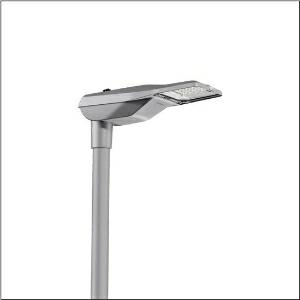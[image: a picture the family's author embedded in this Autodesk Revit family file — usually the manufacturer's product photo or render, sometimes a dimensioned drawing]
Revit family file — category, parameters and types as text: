
# Revit family: streetlight_sl_21_iq_micro___p0_5a_5xe1v31v08cb_beee
name_source: partatom
category: Lighting Fixtures
units: mm (PartAtom-declared; Revit-internal decimal feet)

## family parameters
Cut with Voids When Loaded = No
Host = Face
Light Source = No
Part Type = Normal
Room Calculation Point = No
Round Connector Dimension = Use Diameter
Shared = No

## types (1)
- --- (1 x LED, 2840 lm, 19.1 W, 3000K)
    Apparent Load = 19 VA
    CIE Flux Codes = 37 73 96 100 100
    Color Rendering = 70
    Color Temperature = 3000K
    Default Elevation = 1800 mm
    Description = Streetlight SL 21 iQ micro, mast luminaire, primary light control with lens, of PMMA, primary optical cover: cover, of toughened safety glass, transparent, light distribution: P0.5a, light emission: direct distribution, primary light characteristic: asymmetric, installation type: post-top, side-entry, LED, High Power LED, rated luminous flux: 2.840lm, luminous efficacy: 149lm/W, light colour: 730, colour temperature: 3000K, control gear: iQ-Street Remote, D4i with power reduction, control: pre-setting: logarithmic dimming characteristic, Street-Remote, Auto-Match, Temp-Guard, Lumen-Switch, Night-Set, Smart-Wire, Light-Fading, Desk-Remote (wireless, voltage-free reading and setting of iQ features in the workshop via application-optimized NFC function/RFID function), optimised constant luminous flux control (CLO 2.0), mains connection: 220..240V, AC, 50/60Hz, start of lifetime: 19W, end of service life: 20W, reduction: 9W, luminaire housing, of diecast aluminium, powder-coated, Siteco® metallic grey (DB 702S), corrosivity category C5 mid according to DIN EN ISO 12944, please order mast flange separately, inclination adjustable: 0°, 5°, 10°, 15°, sealing non-destructively replaceable, multi-level sealing system, length: 528mm, width: 235mm, height: 110mm, mast flange for spigot size: 42mm (side-entry): 5XC10008XM4, 60/48mm (side-entry/post-top): 5XC10108XM2, 76/60mm (side-entry/post-top): 5XC10108XM1, mounting height: 4..8m, Smart Interface above, protection rating (complete): IP66, insulation class (complete): insulation class II (safety insulation), certification: CE, ENEC, ENEC+, VDE, impact resistance: IK09, permissible operating ambient temperature for outdoor applications: -40..+50°C, standard-compliant lighting for roads and squares, packaging unit: 1 piece

Light Distribution: P0.5a
    Height = 110 mm
    Lamp = 1 x LED
    Lamp Light Flux = 2840 lm
    Lamp Power = 19.1 W
    Lamp count = 1
    Length = 528 mm
    Luminous efficacy = 149 lm/W
    Manufacturer = Siteco
    ModVariant = No
    Model = 5XE1V31V08CB
    Number of Poles = 1
    OnlyDefault = Yes
    Power Factor = 1
    Product Name = Streetlight SL 21 iQ micro | P0.5a
    Product group = mast luminaire | pylon top
    ProductGroupID = 6100
    Protection Class = Protection class II
    Protection Degree = IP 66
    RLX_Detail_Level = 1
    RLX_Emergency_Light_Flux = 0 lm
    RLX_Emergency_Type = 0
    RLX_Emergency_Type_DB = No
    RlxData = <blob elided: 97949 chars, md5=3381ee49>
    Socket = socket
    Standby Power = 0 W
    System Light Flux = 2840 lm
    System Power = 19 W
    Type Comments = factory setting: luminous flux: 100 % | dim-lin: 254 | 387 mA
    Type Image = l_1277292.jpg
    URL = http://relux.com
    VarID = @adj_067148
    Voltage = 0 V
    Weight = 0.00 kg
    Width = 235 mm

## geometry (parser evidence)
native form markers: Blend x4, Sweep x10
no freeform markers — native parametric forms only
